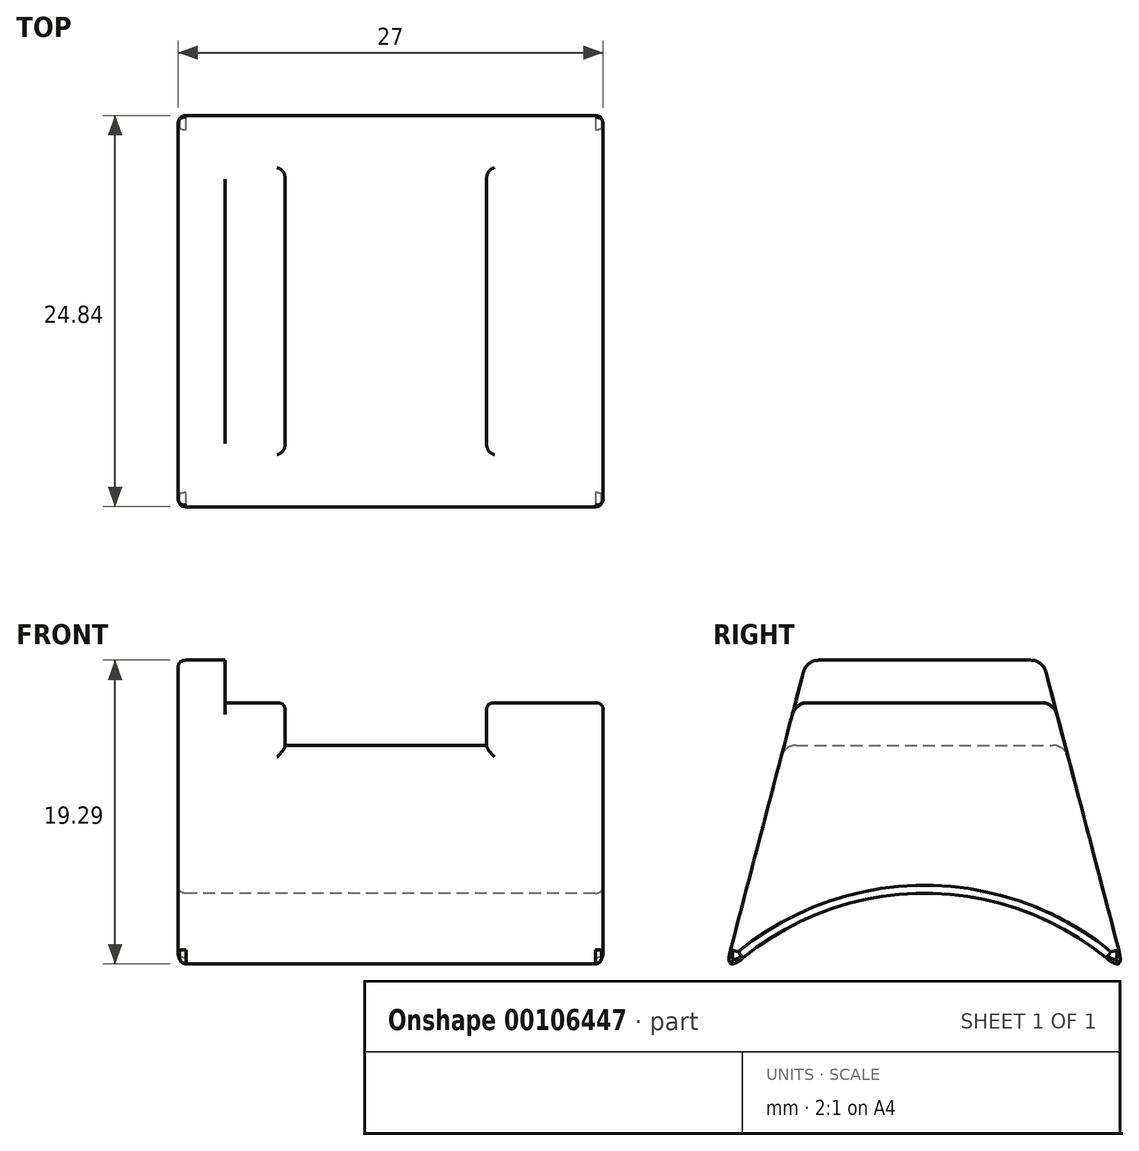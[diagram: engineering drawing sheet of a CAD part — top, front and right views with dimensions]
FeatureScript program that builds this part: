
annotation { "Feature Type Name" : "Feature", "Feature Type Description" : "" }
export const myFeature = defineFeature(function(context is Context, id is Id, definition is map)
    precondition{}
    {
        {
            var Q0;
            Q0=qCreatedBy(makeId("Right.planeOp"),FACE);
            var sketch = newSketch(context, id + "F0", { "sketchPlane" : qUnion([Q0])});
            skLineSegment(sketch, "E0", {"start": v(-7.5, 0) * mm, "end": v(7.5, 0) * mm});
            skArc(sketch, "E1", {"start": v(12.75, -20) * mm, "mid": v(0, -14.8) * mm, "end": v(-12.75, -20) * mm});
            skLineSegment(sketch, "E2", {"start": v(-7.5, 0) * mm, "end": v(-12.75, -20) * mm});
            skLineSegment(sketch, "E3", {"start": v(7.5, 0) * mm, "end": v(12.75, -20) * mm});
            skSolve(sketch);
        }
        {
            var Q0;
            Q0 = qSketchRegion(id + "F0", true);
            var Q1;
            Q1=makeQuery(id+"F0.imprint","IMPRINT",FACE,{"disambiguationData":[TD([[makeQuery(id+"F0.imprint","IMPRINT",EDGE,{"derivedFrom":sQuery(id+"F0.wireOp",EDGE,"E0")}),-1.0]])]});
            extrude(context, id + "F1", {"entities" : qUnion([Q0, Q1]), "endBound" : BoundingType.SYMMETRIC, "depth" : 27 * mm});
        }
        {
            var Q0;
            Q0=qCreatedBy(makeId("Front.planeOp"),FACE);
            var sketch = newSketch(context, id + "F2", { "sketchPlane" : qUnion([Q0])});
            skLineSegment(sketch, "E4", {"start": v(-10.5, 0) * mm, "end": v(-10.5, -2.7) * mm});
            skLineSegment(sketch, "E5", {"start": v(-10.5, -2.7) * mm, "end": v(-6.7, -2.7) * mm});
            skLineSegment(sketch, "E6", {"start": v(-6.7, -2.7) * mm, "end": v(-6.7, -5.4) * mm});
            skLineSegment(sketch, "E7", {"start": v(-6.7, -5.4) * mm, "end": v(6.1, -5.4) * mm});
            skLineSegment(sketch, "E8", {"start": v(6.1, -5.4) * mm, "end": v(6.1, -2.7) * mm});
            skLineSegment(sketch, "E9", {"start": v(6.1, -2.7) * mm, "end": v(13.63, -2.7) * mm});
            skLineSegment(sketch, "E10", {"start": v(13.63, -2.7) * mm, "end": v(13.63, 0) * mm});
            skLineSegment(sketch, "E11", {"start": v(13.63, 0) * mm, "end": v(-10.5, 0) * mm});
            skSolve(sketch);
        }
        {
            var Q0;
            Q0=makeQuery(id+"F2.imprint","IMPRINT",FACE,{"disambiguationData":[TD([[makeQuery(id+"F2.imprint","IMPRINT",EDGE,{"derivedFrom":sQuery(id+"F2.wireOp",EDGE,"E4")}),1.0]])]});
            extrude(context, id + "F3", {"entities" : qUnion([Q0]), "endBound" : BoundingType.SYMMETRIC, "depth" : 25 * mm});
        }
        {
            var Q0;
            Q0=makeQuery(id+"F3.opExtrude","SWEPT_BODY",BODY,{"disambiguationData":[OSD([sQuery(id+"F2.wireOp",EDGE,"E4"),sQuery(id+"F2.wireOp",EDGE,"E5"),sQuery(id+"F2.wireOp",EDGE,"E6"),sQuery(id+"F2.wireOp",EDGE,"E7"),sQuery(id+"F2.wireOp",EDGE,"E8"),sQuery(id+"F2.wireOp",EDGE,"E9"),sQuery(id+"F2.wireOp",EDGE,"E10"),sQuery(id+"F2.wireOp",EDGE,"E11")])]});
            var Q1;
            Q1=makeQuery(id+"F1.opExtrude","SWEPT_BODY",BODY,{"disambiguationData":[OSD([sQuery(id+"F0.wireOp",EDGE,"E0"),sQuery(id+"F0.wireOp",EDGE,"E1"),sQuery(id+"F0.wireOp",EDGE,"E2"),sQuery(id+"F0.wireOp",EDGE,"E3")])]});
            booleanBodies(context, id + "F4", {"operationType" : BooleanOperationType.SUBTRACTION, "tools" : qUnion([Q0]), "targets" : qUnion([Q1])});
        }
        {
            var Q0;
            Q0=makeQuery(id+"F4.opBoolean","INTERSECT",EDGE,{"derivedFrom":[makeQuery(id+"F1.opExtrude","SWEPT_FACE",FACE,{"disambiguationData":[OSD([sQuery(id+"F0.wireOp",EDGE,"E2")])]}),makeQuery(id+"F3.opExtrude","SWEPT_FACE",FACE,{"disambiguationData":[OSD([sQuery(id+"F2.wireOp",EDGE,"E7")])]})]});
            var Q1;
            Q1=makeQuery(id+"F4.opBoolean","INTERSECT",EDGE,{"derivedFrom":[makeQuery(id+"F1.opExtrude","SWEPT_FACE",FACE,{"disambiguationData":[OSD([sQuery(id+"F0.wireOp",EDGE,"E2")])]}),makeQuery(id+"F3.opExtrude","SWEPT_FACE",FACE,{"disambiguationData":[OSD([sQuery(id+"F2.wireOp",EDGE,"E5")])]})]});
            var Q2;
            Q2=makeQuery(id+"F1.opExtrude","SWEPT_EDGE",EDGE,{"disambiguationData":[OSD([sQuery(id+"F0.wireOp",EDGE,"E0"),sQuery(id+"F0.wireOp",EDGE,"E2")])]});
            var Q3;
            Q3=makeQuery(id+"F4.opBoolean","INTERSECT",EDGE,{"derivedFrom":[makeQuery(id+"F1.opExtrude","SWEPT_FACE",FACE,{"disambiguationData":[OSD([sQuery(id+"F0.wireOp",EDGE,"E2")])]}),makeQuery(id+"F3.opExtrude","SWEPT_FACE",FACE,{"disambiguationData":[OSD([sQuery(id+"F2.wireOp",EDGE,"E9")])]})]});
            var Q4;
            Q4=makeQuery(id+"F1.opExtrude","SWEPT_EDGE",EDGE,{"disambiguationData":[OSD([sQuery(id+"F0.wireOp",EDGE,"E0"),sQuery(id+"F0.wireOp",EDGE,"E3")])]});
            var Q5;
            Q5=makeQuery(id+"F4.opBoolean","INTERSECT",EDGE,{"derivedFrom":[makeQuery(id+"F1.opExtrude","SWEPT_FACE",FACE,{"disambiguationData":[OSD([sQuery(id+"F0.wireOp",EDGE,"E3")])]}),makeQuery(id+"F3.opExtrude","SWEPT_FACE",FACE,{"disambiguationData":[OSD([sQuery(id+"F2.wireOp",EDGE,"E5")])]})]});
            var Q6;
            Q6=makeQuery(id+"F4.opBoolean","INTERSECT",EDGE,{"derivedFrom":[makeQuery(id+"F1.opExtrude","SWEPT_FACE",FACE,{"disambiguationData":[OSD([sQuery(id+"F0.wireOp",EDGE,"E3")])]}),makeQuery(id+"F3.opExtrude","SWEPT_FACE",FACE,{"disambiguationData":[OSD([sQuery(id+"F2.wireOp",EDGE,"E7")])]})]});
            var Q7;
            Q7=makeQuery(id+"F4.opBoolean","INTERSECT",EDGE,{"derivedFrom":[makeQuery(id+"F1.opExtrude","SWEPT_FACE",FACE,{"disambiguationData":[OSD([sQuery(id+"F0.wireOp",EDGE,"E3")])]}),makeQuery(id+"F3.opExtrude","SWEPT_FACE",FACE,{"disambiguationData":[OSD([sQuery(id+"F2.wireOp",EDGE,"E9")])]})]});
            fillet(context, id + "F5", {"entities" : qUnion([Q0, Q1, Q2, Q3, Q4, Q5, Q6, Q7]), "radius" : 1 * mm, "tangentPropagation" : true, "allowEdgeOverflow" : false});
        }
        {
            var Q0;
            Q0=makeQuery(id+"F4.opBoolean","INTERSECT",EDGE,{"derivedFrom":[makeQuery(id+"F1.opExtrude","CAP_FACE",FACE,{"disambiguationData":[OSD([sQuery(id+"F0.wireOp",EDGE,"E0"),sQuery(id+"F0.wireOp",EDGE,"E1"),sQuery(id+"F0.wireOp",EDGE,"E2"),sQuery(id+"F0.wireOp",EDGE,"E3")])],"isStart":false}),makeQuery(id+"F3.opExtrude","SWEPT_FACE",FACE,{"disambiguationData":[OSD([sQuery(id+"F2.wireOp",EDGE,"E9")])]})]});
            var Q1;
            Q1=makeQuery(id+"F4.opBoolean","COPY",EDGE,{"derivedFrom":makeQuery(id+"F3.opExtrude","SWEPT_EDGE",EDGE,{"disambiguationData":[OSD([sQuery(id+"F2.wireOp",EDGE,"E5"),sQuery(id+"F2.wireOp",EDGE,"E6")])]})});
            var Q2;
            Q2=makeQuery(id+"F4.opBoolean","COPY",EDGE,{"derivedFrom":makeQuery(id+"F3.opExtrude","SWEPT_EDGE",EDGE,{"disambiguationData":[OSD([sQuery(id+"F2.wireOp",EDGE,"E4"),sQuery(id+"F2.wireOp",EDGE,"E11")])]})});
            var Q3;
            Q3=makeQuery(id+"F1.opExtrude","CAP_EDGE",EDGE,{"disambiguationData":[OSD([sQuery(id+"F0.wireOp",EDGE,"E0")])],"isStart":true});
            var Q4;
            Q4=makeQuery(id+"F4.opBoolean","COPY",EDGE,{"derivedFrom":makeQuery(id+"F3.opExtrude","SWEPT_EDGE",EDGE,{"disambiguationData":[OSD([sQuery(id+"F2.wireOp",EDGE,"E8"),sQuery(id+"F2.wireOp",EDGE,"E9")])]})});
            var Q5;
            Q5=makeQuery(id+"F1.opExtrude","CAP_EDGE",EDGE,{"disambiguationData":[OSD([sQuery(id+"F0.wireOp",EDGE,"E1")])],"isStart":true});
            var Q6;
            Q6=makeQuery(id+"F1.opExtrude","CAP_EDGE",EDGE,{"disambiguationData":[OSD([sQuery(id+"F0.wireOp",EDGE,"E1")])],"isStart":false});
            var Q7;
            Q7=makeQuery(id+"F1.opExtrude","SWEPT_EDGE",EDGE,{"disambiguationData":[OSD([sQuery(id+"F0.wireOp",EDGE,"E1"),sQuery(id+"F0.wireOp",EDGE,"E3")])]});
            var Q8;
            Q8=makeQuery(id+"F1.opExtrude","SWEPT_EDGE",EDGE,{"disambiguationData":[OSD([sQuery(id+"F0.wireOp",EDGE,"E1"),sQuery(id+"F0.wireOp",EDGE,"E2")])]});
            fillet(context, id + "F6", {"entities" : qUnion([Q0, Q1, Q2, Q3, Q4, Q5, Q6, Q7, Q8]), "radius" : 0.5 * mm, "tangentPropagation" : true, "rho" : 0.5, "crossSection" : FilletCrossSection.CONIC, "allowEdgeOverflow" : false});
        }
    });
